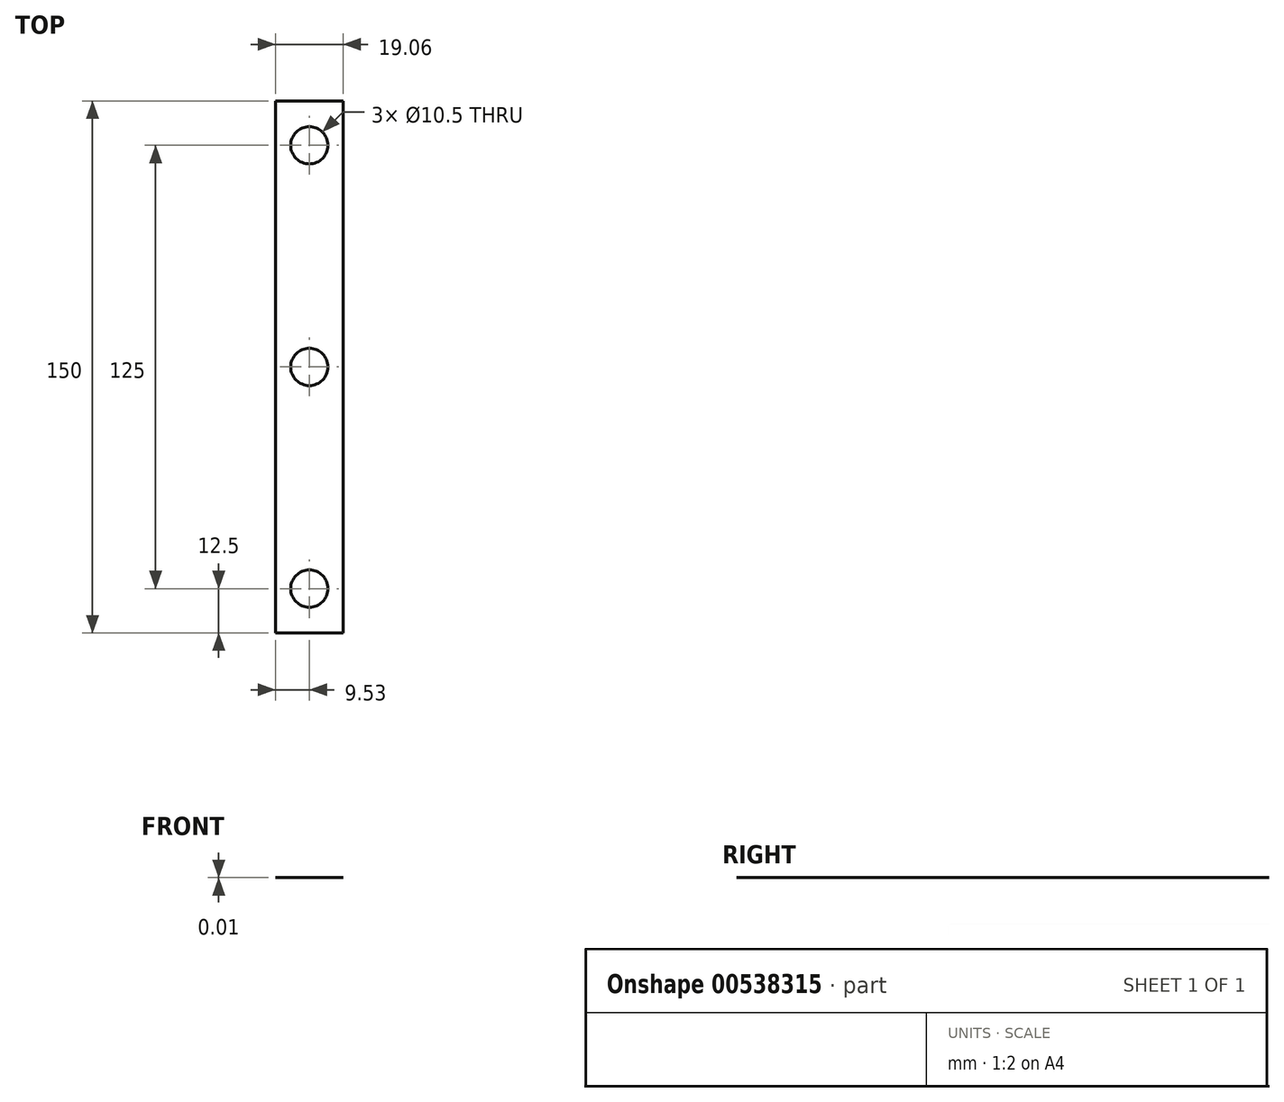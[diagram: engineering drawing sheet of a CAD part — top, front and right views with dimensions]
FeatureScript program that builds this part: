
annotation { "Feature Type Name" : "Feature", "Feature Type Description" : "" }
export const myFeature = defineFeature(function(context is Context, id is Id, definition is map)
    precondition{}
    {
        {
            var Q0;
            Q0=qCreatedBy(makeId("Top.planeOp"),FACE);
            var sketch = newSketch(context, id + "F0", { "sketchPlane" : qUnion([Q0])});
            skLineSegment(sketch, "E0.bottom", {"start": v(9.53, -75) * mm, "end": v(-9.52, -75) * mm});
            skLineSegment(sketch, "E0.top", {"start": v(9.52, 75) * mm, "end": v(-9.53, 75) * mm});
            skLineSegment(sketch, "E0.left", {"start": v(9.53, -75) * mm, "end": v(9.52, 75) * mm});
            skLineSegment(sketch, "E0.right", {"start": v(-9.52, -75) * mm, "end": v(-9.53, 75) * mm});
            skPoint(sketch, "E0.middle", {"position": v(0, 0) * mm});
            skSolve(sketch);
        }
        {
            var Q0;
            Q0 = qSketchRegion(id + "F0", true);
            extrude(context, id + "F1", {"entities" : qUnion([Q0]), "depth" : 3 / 203.2 * mm, "offsetDistance" : 25.4 * mm});
        }
        {
            var Q0;
            Q0=makeQuery(id+"F1.opExtrude","CAP_FACE",FACE,{"disambiguationData":[OSD([sQuery(id+"F0.wireOp",EDGE,"E0.bottom"),sQuery(id+"F0.wireOp",EDGE,"E0.top"),sQuery(id+"F0.wireOp",EDGE,"E0.left"),sQuery(id+"F0.wireOp",EDGE,"E0.right")])],"isStart":false});
            var sketch = newSketch(context, id + "F2", { "sketchPlane" : qUnion([Q0])});
            skLineSegment(sketch, "E1", {"start": v(0, -75) * mm, "end": v(0, 85.22) * mm, "construction": true});
            skPoint(sketch, "E1.endSnap0", {"position": v(0, -75) * mm});
            skLineSegment(sketch, "E2", {"start": v(-9.53, 75) * mm, "end": v(9.52, 75) * mm, "construction": true});
            skLineSegment(sketch, "E3", {"start": v(-9.52, -75) * mm, "end": v(9.53, -75) * mm, "construction": true});
            skLineSegment(sketch, "E4.0", {"start": v(-9.52, -62.5) * mm, "end": v(9.53, -62.5) * mm, "construction": true});
            skLineSegment(sketch, "E5.0", {"start": v(-9.53, 62.5) * mm, "end": v(9.52, 62.5) * mm, "construction": true});
            skCircle(sketch, "E6", {"center": v(0, 62.5) * mm, "radius": 5.25 * mm});
            skCircle(sketch, "E7", {"center": v(0, -62.5) * mm, "radius": 5.25 * mm});
            skSolve(sketch);
        }
        {
            var Q0;
            Q0 = qSketchRegion(id + "F2", true);
            extrude(context, id + "F3", {"entities" : qUnion([Q0]), "operationType" : NewBodyOperationType.REMOVE, "oppositeDirection" : true, "depth" : 25.4 * mm, "offsetDistance" : 25.4 * mm});
        }
        {
            var Q0;
            Q0=makeQuery(id+"F1.opExtrude","CAP_FACE",FACE,{"disambiguationData":[OSD([sQuery(id+"F0.wireOp",EDGE,"E0.bottom"),sQuery(id+"F0.wireOp",EDGE,"E0.top"),sQuery(id+"F0.wireOp",EDGE,"E0.left"),sQuery(id+"F0.wireOp",EDGE,"E0.right")])],"isStart":false});
            var sketch = newSketch(context, id + "F4", { "sketchPlane" : qUnion([Q0])});
            skCircle(sketch, "E8", {"center": v(0, 0) * mm, "radius": 5.25 * mm});
            skSolve(sketch);
        }
        {
            var Q0;
            Q0=makeQuery(id+"F4.imprint","IMPRINT",FACE,{"disambiguationData":[TD([[makeQuery(id+"F4.imprint","IMPRINT",EDGE,{"derivedFrom":sQuery(id+"F4.wireOp",EDGE,"E8")}),1.0]])]});
            extrude(context, id + "F5", {"entities" : qUnion([Q0]), "operationType" : NewBodyOperationType.REMOVE, "oppositeDirection" : true, "depth" : 25.4 * mm, "offsetDistance" : 25.4 * mm});
        }
    });
